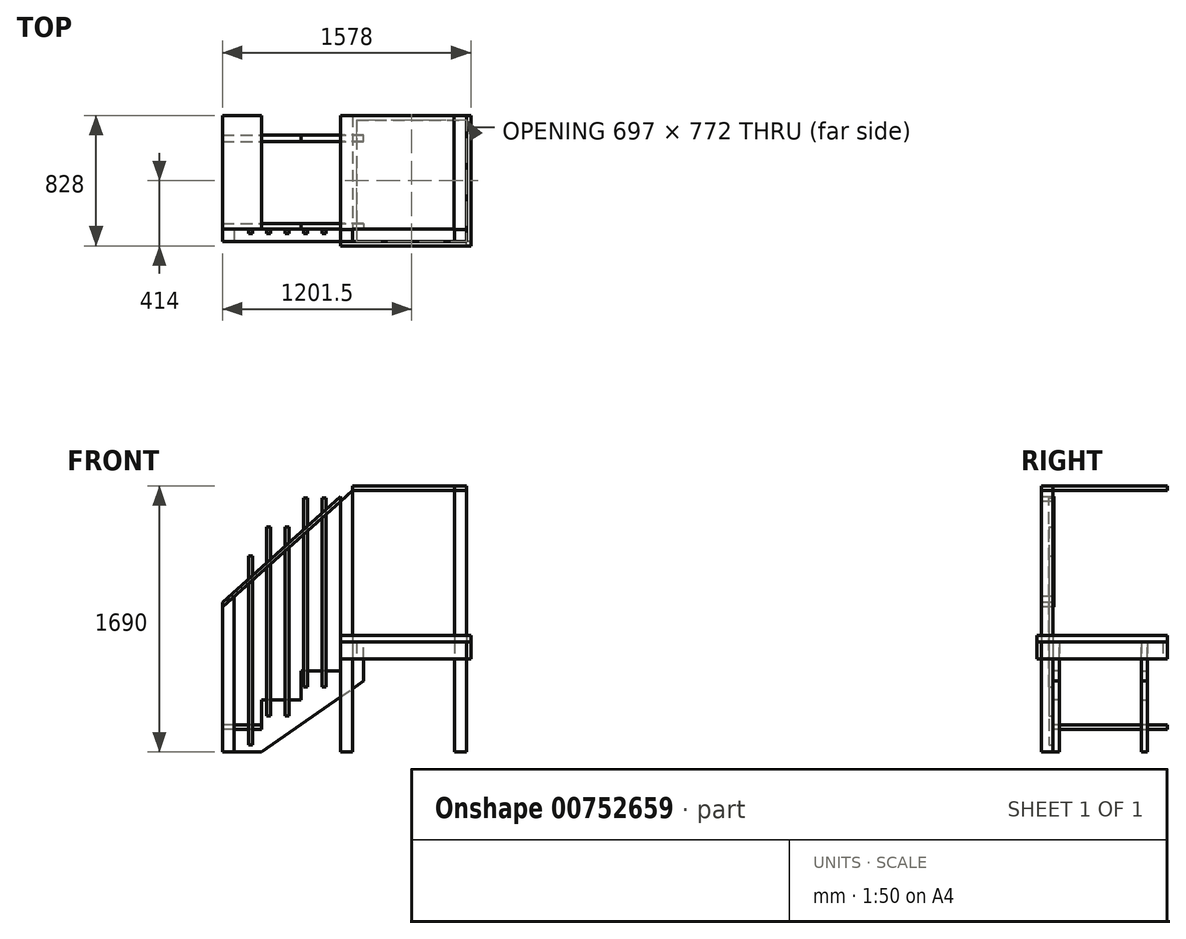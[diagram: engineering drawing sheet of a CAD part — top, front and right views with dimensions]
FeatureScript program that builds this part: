
annotation { "Feature Type Name" : "Feature", "Feature Type Description" : "" }
export const myFeature = defineFeature(function(context is Context, id is Id, definition is map)
    precondition{}
    {
        {
            var Q0;
            Q0=qCreatedBy(makeId("Top.planeOp"),FACE);
            var sketch = newSketch(context, id + "F0", { "sketchPlane" : qUnion([Q0])});
            skLineSegment(sketch, "E0.bottom", {"start": v(0, 0) * mm, "end": v(75, 0) * mm});
            skLineSegment(sketch, "E0.top", {"start": v(0, 75) * mm, "end": v(75, 75) * mm});
            skLineSegment(sketch, "E0.left", {"start": v(0, 0) * mm, "end": v(0, 75) * mm});
            skLineSegment(sketch, "E0.right", {"start": v(75, 0) * mm, "end": v(75, 75) * mm});
            skLineSegment(sketch, "E1.bottom", {"start": v(725, 0) * mm, "end": v(800, 0) * mm});
            skLineSegment(sketch, "E1.top", {"start": v(725, 75) * mm, "end": v(800, 75) * mm});
            skLineSegment(sketch, "E1.left", {"start": v(725, 0) * mm, "end": v(725, 75) * mm});
            skLineSegment(sketch, "E1.right", {"start": v(800, 0) * mm, "end": v(800, 75) * mm});
            skSolve(sketch);
        }
        {
            var Q0;
            Q0 = qSketchRegion(id + "F0", true);
            extrude(context, id + "F1", {"entities" : qUnion([Q0]), "depth" : (700 + 950 + 40) * mm, "offsetDistance" : 25 * mm});
        }
        {
            var Q0;
            Q0=makeQuery(id+"F1.opExtrude","SWEPT_FACE",FACE,{"disambiguationData":[OSD([sQuery(id+"F0.wireOp",EDGE,"E0.bottom")])]});
            var sketch = newSketch(context, id + "F2", { "sketchPlane" : qUnion([Q0])});
            skLineSegment(sketch, "E2.bottom", {"start": v(0, 590) * mm, "end": v(800, 590) * mm});
            skLineSegment(sketch, "E2.top", {"start": v(0, 700) * mm, "end": v(800, 700) * mm});
            skLineSegment(sketch, "E2.left", {"start": v(0, 590) * mm, "end": v(0, 700) * mm});
            skLineSegment(sketch, "E2.right", {"start": v(800, 700) * mm, "end": v(800, 590) * mm});
            skSolve(sketch);
        }
        {
            var Q0;
            Q0 = qSketchRegion(id + "F2", true);
            extrude(context, id + "F3", {"entities" : qUnion([Q0]), "depth" : 28 * mm, "offsetDistance" : 25 * mm});
        }
        {
            var Q0;
            Q0=makeQuery(id+"F1.opExtrude","SWEPT_FACE",FACE,{"disambiguationData":[OSD([sQuery(id+"F0.wireOp",EDGE,"E1.right")])]});
            var sketch = newSketch(context, id + "F4", { "sketchPlane" : qUnion([Q0])});
            skLineSegment(sketch, "E3.bottom", {"start": v(0, 700) * mm, "end": v(800, 700) * mm});
            skLineSegment(sketch, "E3.top", {"start": v(0, 590) * mm, "end": v(800, 590) * mm});
            skLineSegment(sketch, "E3.left", {"start": v(0, 700) * mm, "end": v(0, 590) * mm});
            skLineSegment(sketch, "E3.right", {"start": v(800, 700) * mm, "end": v(800, 590) * mm});
            skSolve(sketch);
        }
        {
            var Q0;
            Q0 = qSketchRegion(id + "F4", true);
            extrude(context, id + "F5", {"entities" : qUnion([Q0]), "operationType" : NewBodyOperationType.ADD, "depth" : 28 * mm, "offsetDistance" : 25 * mm});
        }
        {
            var Q0;
            Q0=makeQuery(id+"F3.opExtrude","CAP_FACE",FACE,{"disambiguationData":[OSD([sQuery(id+"F2.wireOp",EDGE,"E2.bottom"),sQuery(id+"F2.wireOp",EDGE,"E2.top"),sQuery(id+"F2.wireOp",EDGE,"E2.left"),sQuery(id+"F2.wireOp",EDGE,"E2.right")])],"isStart":true});
            var sketch = newSketch(context, id + "F6", { "sketchPlane" : qUnion([Q0])});
            skLineSegment(sketch, "E4.bottom", {"start": v(-75, 700) * mm, "end": v(-103, 700) * mm});
            skLineSegment(sketch, "E4.top", {"start": v(-75, 590) * mm, "end": v(-103, 590) * mm});
            skLineSegment(sketch, "E4.left", {"start": v(-75, 700) * mm, "end": v(-75, 590) * mm});
            skLineSegment(sketch, "E4.right", {"start": v(-103, 700) * mm, "end": v(-103, 590) * mm});
            skSolve(sketch);
        }
        {
            var Q0;
            Q0 = qSketchRegion(id + "F6", true);
            var Q1;
            Q1=makeQuery(id+"F5.opExtrude","SWEPT_FACE",FACE,{"disambiguationData":[OSD([sQuery(id+"F4.wireOp",EDGE,"E3.right")])]});
            extrude(context, id + "F7", {"entities" : qUnion([Q0]), "endBound" : BoundingType.UP_TO_SURFACE, "depth" : 25 * mm, "endBoundEntityFace" : qUnion([Q1]), "offsetDistance" : 25 * mm});
        }
        {
            var Q0;
            Q0=makeQuery(id+"F5.opExtrude","CAP_FACE",FACE,{"disambiguationData":[OSD([sQuery(id+"F4.wireOp",EDGE,"E3.bottom"),sQuery(id+"F4.wireOp",EDGE,"E3.top"),sQuery(id+"F4.wireOp",EDGE,"E3.left"),sQuery(id+"F4.wireOp",EDGE,"E3.right")])],"isStart":true});
            var sketch = newSketch(context, id + "F8", { "sketchPlane" : qUnion([Q0])});
            skLineSegment(sketch, "E5.bottom", {"start": v(-800, 700) * mm, "end": v(-772, 700) * mm});
            skLineSegment(sketch, "E5.top", {"start": v(-800, 590) * mm, "end": v(-772, 590) * mm});
            skLineSegment(sketch, "E5.left", {"start": v(-800, 700) * mm, "end": v(-800, 590) * mm});
            skLineSegment(sketch, "E5.right", {"start": v(-772, 700) * mm, "end": v(-772, 590) * mm});
            skSolve(sketch);
        }
        {
            var Q0;
            Q0 = qSketchRegion(id + "F8", true);
            var Q1;
            Q1=makeQuery(id+"F7.opExtrude","SWEPT_FACE",FACE,{"disambiguationData":[OSD([sQuery(id+"F6.wireOp",EDGE,"E4.right")])]});
            extrude(context, id + "F9", {"entities" : qUnion([Q0]), "operationType" : NewBodyOperationType.ADD, "endBound" : BoundingType.UP_TO_SURFACE, "depth" : 25 * mm, "endBoundEntityFace" : qUnion([Q1]), "offsetDistance" : 25 * mm});
        }
        {
            var Q0;
            Q0=makeQuery(id+"F9.boolean.opBoolean","MERGE",FACE,{"derivedFrom":[makeQuery(id+"F5.opExtrude","SWEPT_FACE",FACE,{"disambiguationData":[OSD([sQuery(id+"F4.wireOp",EDGE,"E3.bottom")])]}),makeQuery(id+"F9.opExtrude","SWEPT_FACE",FACE,{"disambiguationData":[OSD([sQuery(id+"F8.wireOp",EDGE,"E5.bottom")])]})]});
            var sketch = newSketch(context, id + "F10", { "sketchPlane" : qUnion([Q0])});
            skLineSegment(sketch, "E6.bottom", {"start": v(828, 800) * mm, "end": v(0, 800) * mm});
            skLineSegment(sketch, "E6.top", {"start": v(828, -28) * mm, "end": v(0, -28) * mm});
            skLineSegment(sketch, "E6.left", {"start": v(828, 800) * mm, "end": v(828, -28) * mm});
            skLineSegment(sketch, "E6.right", {"start": v(0, 800) * mm, "end": v(0, -28) * mm});
            skSolve(sketch);
        }
        {
            var Q0;
            Q0 = qSketchRegion(id + "F10", true);
            extrude(context, id + "F11", {"entities" : qUnion([Q0]), "depth" : 40 * mm, "offsetDistance" : 25 * mm});
        }
        {
            var Q0;
            Q0=makeQuery(id+"F1.opExtrude","SWEPT_FACE",FACE,{"disambiguationData":[OSD([sQuery(id+"F0.wireOp",EDGE,"E0.top")])]});
            cPlane(context, id + "F12", {"entities" : qUnion([Q0]), "cplaneType" : CPlaneType.OFFSET, "offset" : 0 * mm, "width" : 150 * mm, "height" : 150 * mm});
        }
        {
            var Q0;
            Q0=qCreatedBy(id+"F12.planeOp",FACE);
            cPlane(context, id + "F13", {"entities" : qUnion([Q0]), "cplaneType" : CPlaneType.OFFSET, "offset" : 300 * mm, "width" : 150 * mm, "height" : 150 * mm});
        }
        {
            var Q0;
            Q0=qCreatedBy(id+"F12.planeOp",FACE);
            var sketch = newSketch(context, id + "F14", { "sketchPlane" : qUnion([Q0])});
            skLineSegment(sketch, "E7", {"start": v(-145, 700) * mm, "end": v(0, 700) * mm});
            skLineSegment(sketch, "E8", {"start": v(0, 700) * mm, "end": v(0, 515) * mm});
            skLineSegment(sketch, "E9", {"start": v(0, 515) * mm, "end": v(250, 515) * mm});
            skLineSegment(sketch, "E10", {"start": v(250, 515) * mm, "end": v(250, 330) * mm});
            skLineSegment(sketch, "E11", {"start": v(250, 330) * mm, "end": v(500, 330) * mm});
            skLineSegment(sketch, "E12", {"start": v(500, 330) * mm, "end": v(500, 145) * mm});
            skLineSegment(sketch, "E13", {"start": v(500, 145) * mm, "end": v(750, 145) * mm});
            skLineSegment(sketch, "E14", {"start": v(750, 145) * mm, "end": v(750, 0) * mm});
            skLineSegment(sketch, "E15", {"start": v(750, 0) * mm, "end": v(500, 0) * mm});
            skLineSegment(sketch, "E16", {"start": v(500, 0) * mm, "end": v(-145, 450) * mm});
            skLineSegment(sketch, "E17", {"start": v(-145, 450) * mm, "end": v(-145, 700) * mm});
            skSolve(sketch);
        }
        {
            var Q0;
            Q0 = qSketchRegion(id + "F14", true);
            extrude(context, id + "F15", {"entities" : qUnion([Q0]), "depth" : 40 * mm, "offsetDistance" : 25 * mm});
        }
        {
            var Q0;
            Q0=makeQuery(id+"F15.opExtrude","SWEPT_BODY",BODY,{"disambiguationData":[OSD([sQuery(id+"F14.wireOp",EDGE,"E7"),sQuery(id+"F14.wireOp",EDGE,"E8"),sQuery(id+"F14.wireOp",EDGE,"E9"),sQuery(id+"F14.wireOp",EDGE,"E10"),sQuery(id+"F14.wireOp",EDGE,"E11"),sQuery(id+"F14.wireOp",EDGE,"E12"),sQuery(id+"F14.wireOp",EDGE,"E13"),sQuery(id+"F14.wireOp",EDGE,"E14"),sQuery(id+"F14.wireOp",EDGE,"E15"),sQuery(id+"F14.wireOp",EDGE,"E16"),sQuery(id+"F14.wireOp",EDGE,"E17")])]});
            var Q1;
            Q1=qCreatedBy(id+"F13.planeOp",FACE);
            mirror(context, id + "F16", {"entities" : qUnion([Q0]), "mirrorPlane" : qUnion([Q1])});
        }
        {
            var Q0;
            Q0=makeQuery(id+"F15.opExtrude","SWEPT_FACE",FACE,{"disambiguationData":[OSD([sQuery(id+"F14.wireOp",EDGE,"E15")])]});
            var sketch = newSketch(context, id + "F17", { "sketchPlane" : qUnion([Q0])});
            skLineSegment(sketch, "E18.bottom", {"start": v(-750, -75) * mm, "end": v(-675, -75) * mm});
            skLineSegment(sketch, "E18.top", {"start": v(-750, 0) * mm, "end": v(-675, 0) * mm});
            skLineSegment(sketch, "E18.left", {"start": v(-750, -75) * mm, "end": v(-750, 0) * mm});
            skLineSegment(sketch, "E18.right", {"start": v(-675, -75) * mm, "end": v(-675, 0) * mm});
            skSolve(sketch);
        }
        {
            var Q0;
            Q0 = qSketchRegion(id + "F17", true);
            extrude(context, id + "F18", {"entities" : qUnion([Q0]), "operationType" : NewBodyOperationType.ADD, "oppositeDirection" : true, "depth" : 1000 * mm, "offsetDistance" : 25 * mm});
        }
        {
            var Q0;
            Q0=makeQuery(id+"F18.opExtrude","SWEPT_FACE",FACE,{"disambiguationData":[OSD([sQuery(id+"F17.wireOp",EDGE,"E18.top")])]});
            var sketch = newSketch(context, id + "F19", { "sketchPlane" : qUnion([Q0])});
            skLineSegment(sketch, "E19", {"start": v(-750, 920) * mm, "end": v(-675, 987.27) * mm});
            skLineSegment(sketch, "E20", {"start": v(-675, 987.27) * mm, "end": v(-675, 1000) * mm});
            skLineSegment(sketch, "E21", {"start": v(-675, 1000) * mm, "end": v(-750, 1000) * mm});
            skLineSegment(sketch, "E22", {"start": v(-750, 1000) * mm, "end": v(-750, 920) * mm});
            skSolve(sketch);
        }
        {
            var Q0;
            Q0 = qSketchRegion(id + "F19", true);
            var Q1;
            Q1=makeQuery(id+"F18.opExtrude","SWEPT_FACE",FACE,{"disambiguationData":[OSD([sQuery(id+"F17.wireOp",EDGE,"E18.bottom")])]});
            extrude(context, id + "F20", {"entities" : qUnion([Q0]), "operationType" : NewBodyOperationType.REMOVE, "endBound" : BoundingType.UP_TO_SURFACE, "oppositeDirection" : true, "depth" : 25 * mm, "endBoundEntityFace" : qUnion([Q1]), "offsetDistance" : 25 * mm});
        }
        {
            var Q0;
            Q0=makeQuery(id+"F18.opExtrude","SWEPT_FACE",FACE,{"disambiguationData":[OSD([sQuery(id+"F17.wireOp",EDGE,"E18.top")])]});
            var sketch = newSketch(context, id + "F21", { "sketchPlane" : qUnion([Q0])});
            skLineSegment(sketch, "E23", {"start": v(-750, 950) * mm, "end": v(75, 1690) * mm});
            skLineSegment(sketch, "E24", {"start": v(75, 1690) * mm, "end": v(75, 1660) * mm});
            skLineSegment(sketch, "E25", {"start": v(75, 1660) * mm, "end": v(-750, 920) * mm});
            skLineSegment(sketch, "E26", {"start": v(-750, 920) * mm, "end": v(-750, 950) * mm});
            skSolve(sketch);
        }
        {
            var Q0;
            Q0 = qSketchRegion(id + "F21", true);
            extrude(context, id + "F22", {"entities" : qUnion([Q0]), "oppositeDirection" : true, "depth" : 80 * mm, "offsetDistance" : 25 * mm});
        }
        {
            var Q0;
            Q0=makeQuery(id+"F1.opExtrude","SWEPT_FACE",FACE,{"disambiguationData":[OSD([sQuery(id+"F0.wireOp",EDGE,"E0.bottom")])]});
            var sketch = newSketch(context, id + "F23", { "sketchPlane" : qUnion([Q0])});
            skLineSegment(sketch, "E27", {"start": v(0, 1592.73) * mm, "end": v(75, 1660) * mm});
            skLineSegment(sketch, "E28", {"start": v(75, 1660) * mm, "end": v(75, 1690) * mm});
            skLineSegment(sketch, "E29", {"start": v(75, 1690) * mm, "end": v(0, 1690) * mm});
            skLineSegment(sketch, "E30", {"start": v(0, 1690) * mm, "end": v(0, 1592.73) * mm});
            skSolve(sketch);
        }
        {
            var Q0;
            Q0 = qSketchRegion(id + "F23", true);
            extrude(context, id + "F24", {"entities" : qUnion([Q0]), "operationType" : NewBodyOperationType.REMOVE, "endBound" : BoundingType.THROUGH_ALL, "oppositeDirection" : true, "depth" : 25 * mm, "offsetDistance" : 25 * mm});
        }
        {
            var Q0;
            Q0=makeQuery(id+"F15.opExtrude","CAP_FACE",FACE,{"disambiguationData":[OSD([sQuery(id+"F14.wireOp",EDGE,"E7"),sQuery(id+"F14.wireOp",EDGE,"E8"),sQuery(id+"F14.wireOp",EDGE,"E9"),sQuery(id+"F14.wireOp",EDGE,"E10"),sQuery(id+"F14.wireOp",EDGE,"E11"),sQuery(id+"F14.wireOp",EDGE,"E12"),sQuery(id+"F14.wireOp",EDGE,"E13"),sQuery(id+"F14.wireOp",EDGE,"E14"),sQuery(id+"F14.wireOp",EDGE,"E15"),sQuery(id+"F14.wireOp",EDGE,"E16"),sQuery(id+"F14.wireOp",EDGE,"E17")])],"isStart":true});
            var sketch = newSketch(context, id + "F25", { "sketchPlane" : qUnion([Q0])});
            skLineSegment(sketch, "E31.bottom", {"start": v(-326, 230) * mm, "end": v(-351, 230) * mm});
            skLineSegment(sketch, "E31.top", {"start": v(-326, 1430) * mm, "end": v(-351, 1430) * mm});
            skLineSegment(sketch, "E31.left", {"start": v(-326, 230) * mm, "end": v(-326, 1430) * mm});
            skLineSegment(sketch, "E31.right", {"start": v(-351, 230) * mm, "end": v(-351, 1430) * mm});
            skLineSegment(sketch, "E32.bottom", {"start": v(-209, 415) * mm, "end": v(-234, 415) * mm});
            skLineSegment(sketch, "E32.top", {"start": v(-209, 1615) * mm, "end": v(-234, 1615) * mm});
            skLineSegment(sketch, "E32.left", {"start": v(-209, 415) * mm, "end": v(-209, 1615) * mm});
            skLineSegment(sketch, "E32.right", {"start": v(-234, 415) * mm, "end": v(-234, 1615) * mm});
            skLineSegment(sketch, "E33.bottom", {"start": v(-92, 415) * mm, "end": v(-117, 415) * mm});
            skLineSegment(sketch, "E33.top", {"start": v(-92, 1615) * mm, "end": v(-117, 1615) * mm});
            skLineSegment(sketch, "E33.left", {"start": v(-92, 415) * mm, "end": v(-92, 1615) * mm});
            skLineSegment(sketch, "E33.right", {"start": v(-117, 415) * mm, "end": v(-117, 1615) * mm});
            skLineSegment(sketch, "E34.bottom", {"start": v(-468, 1430) * mm, "end": v(-443, 1430) * mm});
            skLineSegment(sketch, "E34.top", {"start": v(-468, 230) * mm, "end": v(-443, 230) * mm});
            skLineSegment(sketch, "E34.left", {"start": v(-468, 1430) * mm, "end": v(-468, 230) * mm});
            skLineSegment(sketch, "E34.right", {"start": v(-443, 1430) * mm, "end": v(-443, 230) * mm});
            skLineSegment(sketch, "E35.bottom", {"start": v(-585, 1245) * mm, "end": v(-560, 1245) * mm});
            skLineSegment(sketch, "E35.top", {"start": v(-585, 45) * mm, "end": v(-560, 45) * mm});
            skLineSegment(sketch, "E35.left", {"start": v(-585, 1245) * mm, "end": v(-585, 45) * mm});
            skLineSegment(sketch, "E35.right", {"start": v(-560, 1245) * mm, "end": v(-560, 45) * mm});
            skSolve(sketch);
        }
        {
            var Q0;
            Q0 = qSketchRegion(id + "F25", true);
            extrude(context, id + "F26", {"entities" : qUnion([Q0]), "depth" : 25 * mm, "offsetDistance" : 25 * mm});
        }
        {
            var Q0;
            Q0=makeQuery(id+"F1.opExtrude","CAP_FACE",FACE,{"disambiguationData":[OSD([sQuery(id+"F0.wireOp",EDGE,"E1.bottom"),sQuery(id+"F0.wireOp",EDGE,"E1.top"),sQuery(id+"F0.wireOp",EDGE,"E1.left"),sQuery(id+"F0.wireOp",EDGE,"E1.right")])],"isStart":false});
            var sketch = newSketch(context, id + "F27", { "sketchPlane" : qUnion([Q0])});
            skLineSegment(sketch, "E36", {"start": v(720, 800) * mm, "end": v(800, 800) * mm});
            skLineSegment(sketch, "E37", {"start": v(800, 800) * mm, "end": v(800, 0) * mm});
            skLineSegment(sketch, "E38", {"start": v(800, 0) * mm, "end": v(725, 0) * mm});
            skLineSegment(sketch, "E39", {"start": v(725, 0) * mm, "end": v(75, 0) * mm});
            skLineSegment(sketch, "E40", {"start": v(75, 0) * mm, "end": v(75, 80) * mm});
            skLineSegment(sketch, "E41", {"start": v(75, 80) * mm, "end": v(720, 80) * mm});
            skLineSegment(sketch, "E42", {"start": v(720, 80) * mm, "end": v(720, 800) * mm});
            skSolve(sketch);
        }
        {
            var Q0;
            Q0 = qSketchRegion(id + "F27", true);
            extrude(context, id + "F28", {"entities" : qUnion([Q0]), "oppositeDirection" : true, "depth" : 30 * mm, "offsetDistance" : 25 * mm});
        }
        {
            var Q0;
            Q0=makeQuery(id+"F15.opExtrude","SWEPT_FACE",FACE,{"disambiguationData":[OSD([sQuery(id+"F14.wireOp",EDGE,"E13")])]});
            var sketch = newSketch(context, id + "F29", { "sketchPlane" : qUnion([Q0])});
            skLineSegment(sketch, "E43.bottom", {"start": v(-500, 75) * mm, "end": v(-750, 75) * mm});
            skLineSegment(sketch, "E43.top", {"start": v(-500, 800) * mm, "end": v(-750, 800) * mm});
            skLineSegment(sketch, "E43.left", {"start": v(-500, 75) * mm, "end": v(-500, 800) * mm});
            skLineSegment(sketch, "E43.right", {"start": v(-750, 75) * mm, "end": v(-750, 800) * mm});
            skSolve(sketch);
        }
        {
            var Q0;
            Q0 = qSketchRegion(id + "F29", true);
            extrude(context, id + "F30", {"entities" : qUnion([Q0]), "depth" : 28 * mm, "offsetDistance" : 25 * mm});
        }
    });
